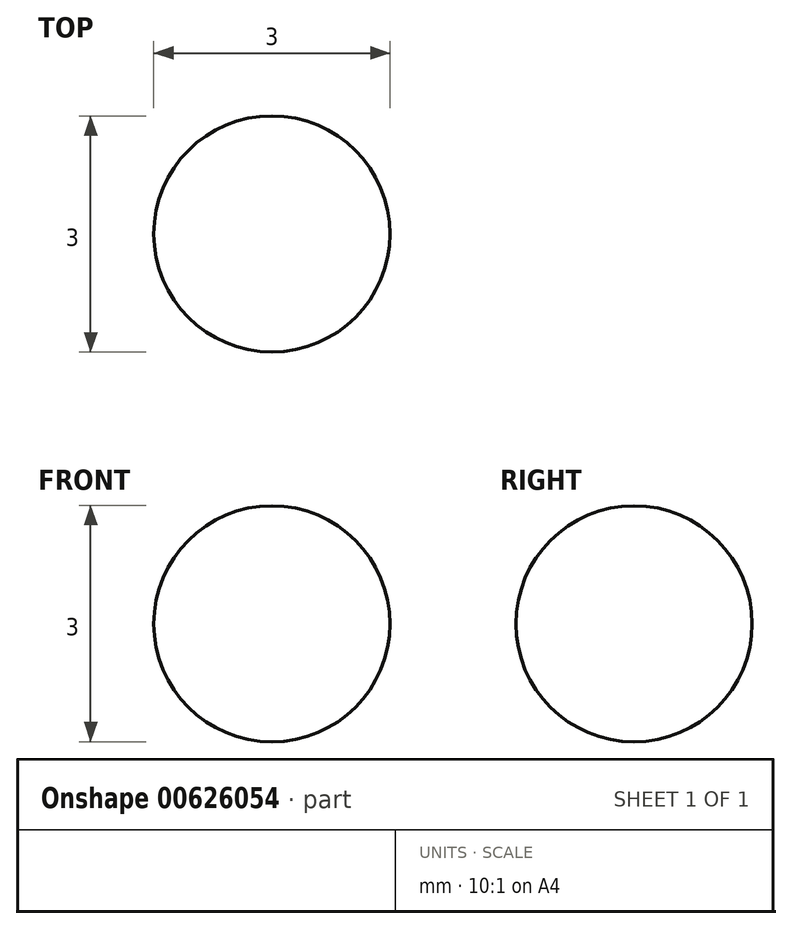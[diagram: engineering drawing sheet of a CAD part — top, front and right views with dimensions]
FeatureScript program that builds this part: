
annotation { "Feature Type Name" : "Feature", "Feature Type Description" : "" }
export const myFeature = defineFeature(function(context is Context, id is Id, definition is map)
    precondition{}
    {
        {
            var Q0;
            Q0=qCreatedBy(makeId("Front.planeOp"),FACE);
            var sketch = newSketch(context, id + "F0", { "sketchPlane" : qUnion([Q0])});
            skLineSegment(sketch, "E0", {"start": v(0, 1.52) * mm, "end": v(0, -1.48) * mm});
            skArc(sketch, "E1", {"start": v(0, -1.48) * mm, "mid": v(1.5, 0.02) * mm, "end": v(0, 1.52) * mm});
            skSolve(sketch);
        }
        {
            var Q0;
            Q0=makeQuery(id+"F0.imprint","IMPRINT",FACE,{"disambiguationData":[TD([[makeQuery(id+"F0.imprint","IMPRINT",EDGE,{"derivedFrom":sQuery(id+"F0.wireOp",EDGE,"E0")}),1.0]])]});
            var Q1;
            Q1=sQuery(id+"F0.wireOp",EDGE,"E0");
            revolve(context, id + "F1", {"entities" : qUnion([Q0]), "axis" : qUnion([Q1]), "revolveType" : RevolveType.FULL});
        }
    });
